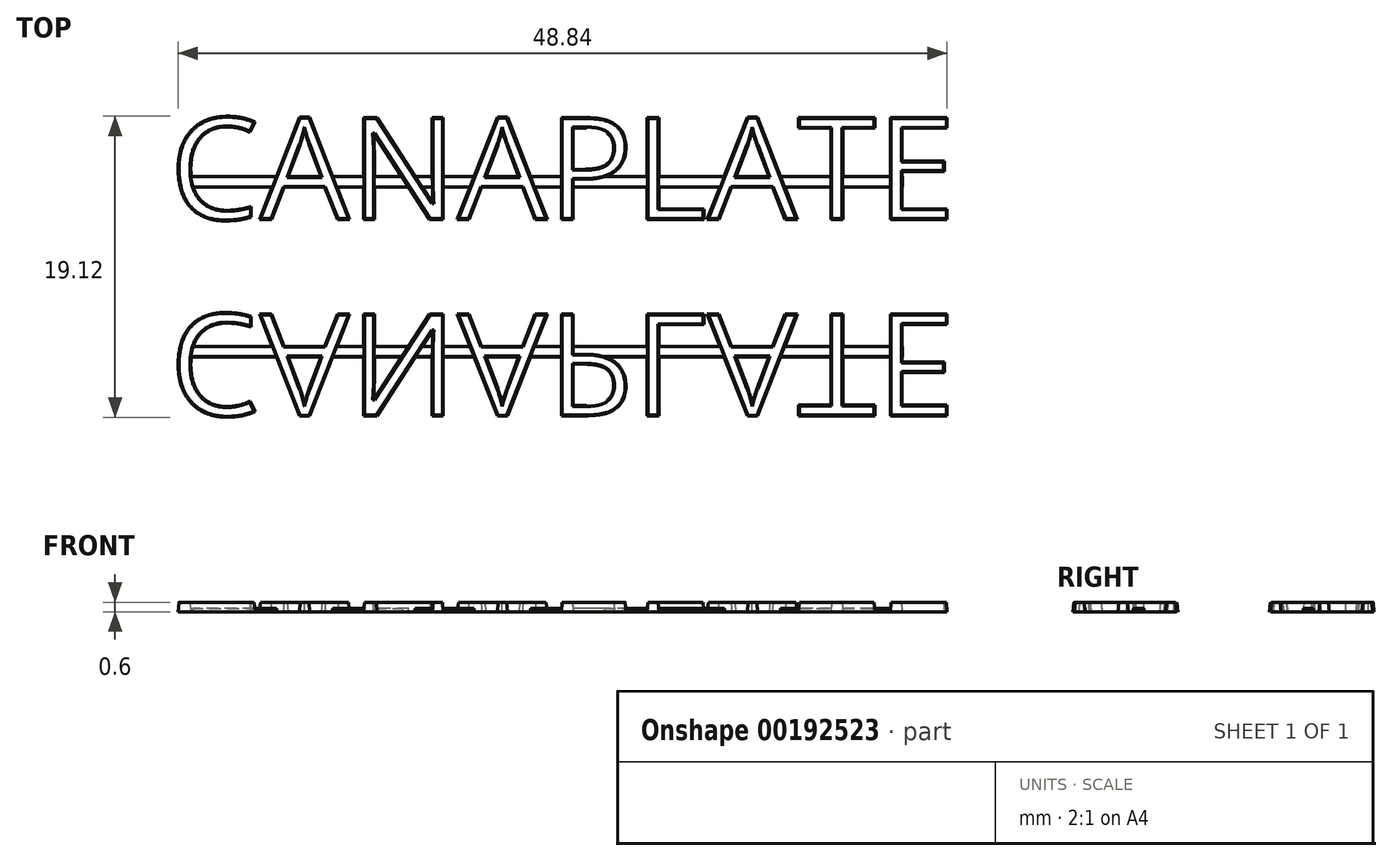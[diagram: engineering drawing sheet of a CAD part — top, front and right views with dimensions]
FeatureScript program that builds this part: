
annotation { "Feature Type Name" : "Feature", "Feature Type Description" : "" }
export const myFeature = defineFeature(function(context is Context, id is Id, definition is map)
    precondition{}
    {
        {
            var Q0;
            Q0=qCreatedBy(makeId("Top.planeOp"),FACE);
            var sketch = newSketch(context, id + "F0", { "sketchPlane" : qUnion([Q0])});
            skText(sketch, "E0", { "text": "CANAPLATE", "fontName": "OpenSans-Regular.ttf"});
            skLineSegment(sketch, "E1", {"start": v(-25, 3) * mm, "end": v(25, 9.52) * mm, "construction": true});
            const initialGuessF0  = {"E0": [-0.025, 0.003, 1, 0, 0.00652]};
            skSetInitialGuess(sketch, initialGuessF0);
            skSolve(sketch);
        }
        {
            var Q0;
            Q0 = qSketchRegion(id + "F0", true);
            extrude(context, id + "F1", {"entities" : qUnion([Q0]), "depth" : 0.6 * mm, "hasDraft" : true, "draftAngle" : 5 * degree, "draftPullDirection" : true});
        }
        {
            var Q0;
            Q0=qCreatedBy(makeId("Top.planeOp"),FACE);
            var sketch = newSketch(context, id + "F2", { "sketchPlane" : qUnion([Q0])});
            skLineSegment(sketch, "E2.bottom", {"start": v(21.56, 5.73) * mm, "end": v(-23.64, 5.73) * mm});
            skLineSegment(sketch, "E2.top", {"start": v(21.56, 5.06) * mm, "end": v(-23.64, 5.06) * mm});
            skLineSegment(sketch, "E2.left", {"start": v(21.56, 5.73) * mm, "end": v(21.56, 5.06) * mm});
            skLineSegment(sketch, "E2.right", {"start": v(-23.64, 5.73) * mm, "end": v(-23.64, 5.06) * mm});
            skSolve(sketch);
        }
        {
            var Q0;
            Q0 = qSketchRegion(id + "F2", true);
            extrude(context, id + "F3", {"entities" : qUnion([Q0]), "operationType" : NewBodyOperationType.ADD, "depth" : 0.2 * mm, "hasDraft" : true, "draftAngle" : 5 * degree, "draftPullDirection" : true});
        }
        {
            var Q0;
            Q0=makeQuery(id+"F1.opExtrude","SWEPT_BODY",BODY,{"disambiguationData":[OSD([sQuery(id+"F0.wireOp",EDGE,"E0.sketch_text.stroke-0"),sQuery(id+"F0.wireOp",EDGE,"E0.sketch_text.stroke-1"),sQuery(id+"F0.wireOp",EDGE,"E0.sketch_text.stroke-2"),sQuery(id+"F0.wireOp",EDGE,"E0.sketch_text.stroke-3"),sQuery(id+"F0.wireOp",EDGE,"E0.sketch_text.stroke-4"),sQuery(id+"F0.wireOp",EDGE,"E0.sketch_text.stroke-5"),sQuery(id+"F0.wireOp",EDGE,"E0.sketch_text.stroke-6"),sQuery(id+"F0.wireOp",EDGE,"E0.sketch_text.stroke-7"),sQuery(id+"F0.wireOp",EDGE,"E0.sketch_text.stroke-8"),sQuery(id+"F0.wireOp",EDGE,"E0.sketch_text.stroke-9"),sQuery(id+"F0.wireOp",EDGE,"E0.sketch_text.stroke-10"),sQuery(id+"F0.wireOp",EDGE,"E0.sketch_text.stroke-11"),sQuery(id+"F0.wireOp",EDGE,"E0.sketch_text.stroke-12"),sQuery(id+"F0.wireOp",EDGE,"E0.sketch_text.stroke-13"),sQuery(id+"F0.wireOp",EDGE,"E0.sketch_text.stroke-14")])]});
            var Q1;
            Q1=qCreatedBy(makeId("Front.planeOp"),FACE);
            mirror(context, id + "F4", {"entities" : qUnion([Q0]), "mirrorPlane" : qUnion([Q1])});
        }
    });
